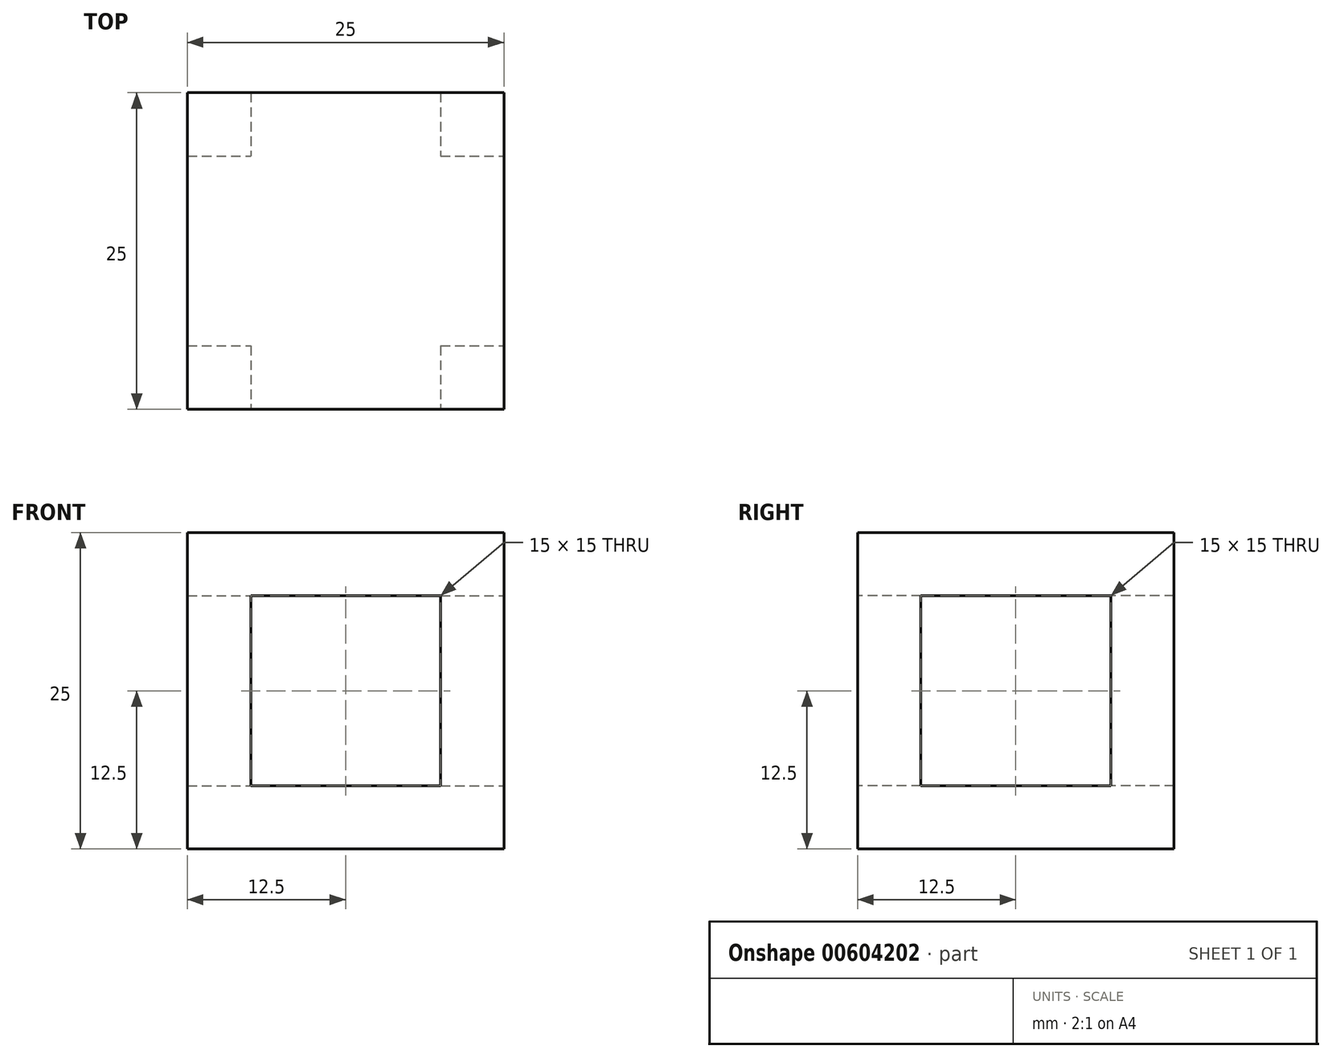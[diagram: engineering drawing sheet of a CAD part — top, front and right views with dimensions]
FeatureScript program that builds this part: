
annotation { "Feature Type Name" : "Feature", "Feature Type Description" : "" }
export const myFeature = defineFeature(function(context is Context, id is Id, definition is map)
    precondition{}
    {
        {
            var Q0;
            Q0=qCreatedBy(makeId("Top.planeOp"),FACE);
            var sketch = newSketch(context, id + "F0", { "sketchPlane" : qUnion([Q0])});
            skLineSegment(sketch, "E0.bottom", {"start": v(-12.5, 12.5) * mm, "end": v(12.5, 12.5) * mm});
            skLineSegment(sketch, "E0.top", {"start": v(-12.5, -12.5) * mm, "end": v(12.5, -12.5) * mm});
            skLineSegment(sketch, "E0.left", {"start": v(-12.5, 12.5) * mm, "end": v(-12.5, -12.5) * mm});
            skLineSegment(sketch, "E0.right", {"start": v(12.5, 12.5) * mm, "end": v(12.5, -12.5) * mm});
            skSolve(sketch);
        }
        {
            var Q0;
            Q0=qSketchRegion(id+"F0",true);
            extrude(context, id + "F1", {"entities" : qUnion([Q0]), "depth" : 25 * mm, "offsetDistance" : 25 * mm});
        }
        {
            var Q0;
            Q0=makeQuery(id+"F1.opExtrude","SWEPT_BODY",BODY,{"disambiguationData":[OSD([sQuery(id+"F0.wireOp",EDGE,"E0.bottom"),sQuery(id+"F0.wireOp",EDGE,"E0.top"),sQuery(id+"F0.wireOp",EDGE,"E0.left"),sQuery(id+"F0.wireOp",EDGE,"E0.right")])]});
            transform(context, id + "F2", {"entities" : qUnion([Q0]), "transformType" : TransformType.TRANSLATION_3D, "dx" : 0 * mm, "dy" : 0 * mm, "dz" : 0 * mm, "makeCopy" : true});
        }
        {
            var Q0;
            Q0=makeQuery(id+"F2.opPattern","COPY",BODY,{"derivedFrom":makeQuery(id+"F1.opExtrude","SWEPT_BODY",BODY,{"disambiguationData":[OSD([sQuery(id+"F0.wireOp",EDGE,"E0.bottom"),sQuery(id+"F0.wireOp",EDGE,"E0.top"),sQuery(id+"F0.wireOp",EDGE,"E0.left"),sQuery(id+"F0.wireOp",EDGE,"E0.right")])]}),"instanceName":"1"});
            deleteBodies(context, id + "F3", {"entities" : qUnion([Q0])});
        }
        {
            var Q0;
            Q0=makeQuery(id+"F1.opExtrude","SWEPT_FACE",FACE,{"disambiguationData":[OSD([sQuery(id+"F0.wireOp",EDGE,"E0.top")])]});
            var Q1;
            Q1=makeQuery(id+"F1.opExtrude","SWEPT_FACE",FACE,{"disambiguationData":[OSD([sQuery(id+"F0.wireOp",EDGE,"E0.bottom")])]});
            shell(context, id + "F4", {"entities" : qUnion([Q0, Q1]), "thickness" : 5 * mm});
        }
        {
            var Q0;
            Q0=makeQuery(id+"F1.opExtrude","SWEPT_FACE",FACE,{"disambiguationData":[OSD([sQuery(id+"F0.wireOp",EDGE,"E0.right")])]});
            var Q1;
            Q1=makeQuery(id+"F1.opExtrude","SWEPT_FACE",FACE,{"disambiguationData":[OSD([sQuery(id+"F0.wireOp",EDGE,"E0.left")])]});
            var Q2;
            Q2=makeQuery(id+"F4.opShell","OFFSET_FACE",FACE,{"disambiguationData":[OSD([sQuery(id+"F0.wireOp",EDGE,"E0.left")])]});
            var Q3;
            Q3=makeQuery(id+"F4.opShell","OFFSET_FACE",FACE,{"disambiguationData":[OSD([sQuery(id+"F0.wireOp",EDGE,"E0.right")])]});
            shell(context, id + "F5", {"entities" : qUnion([Q0, Q1, Q2, Q3]), "thickness" : 5 * mm});
        }
    });
